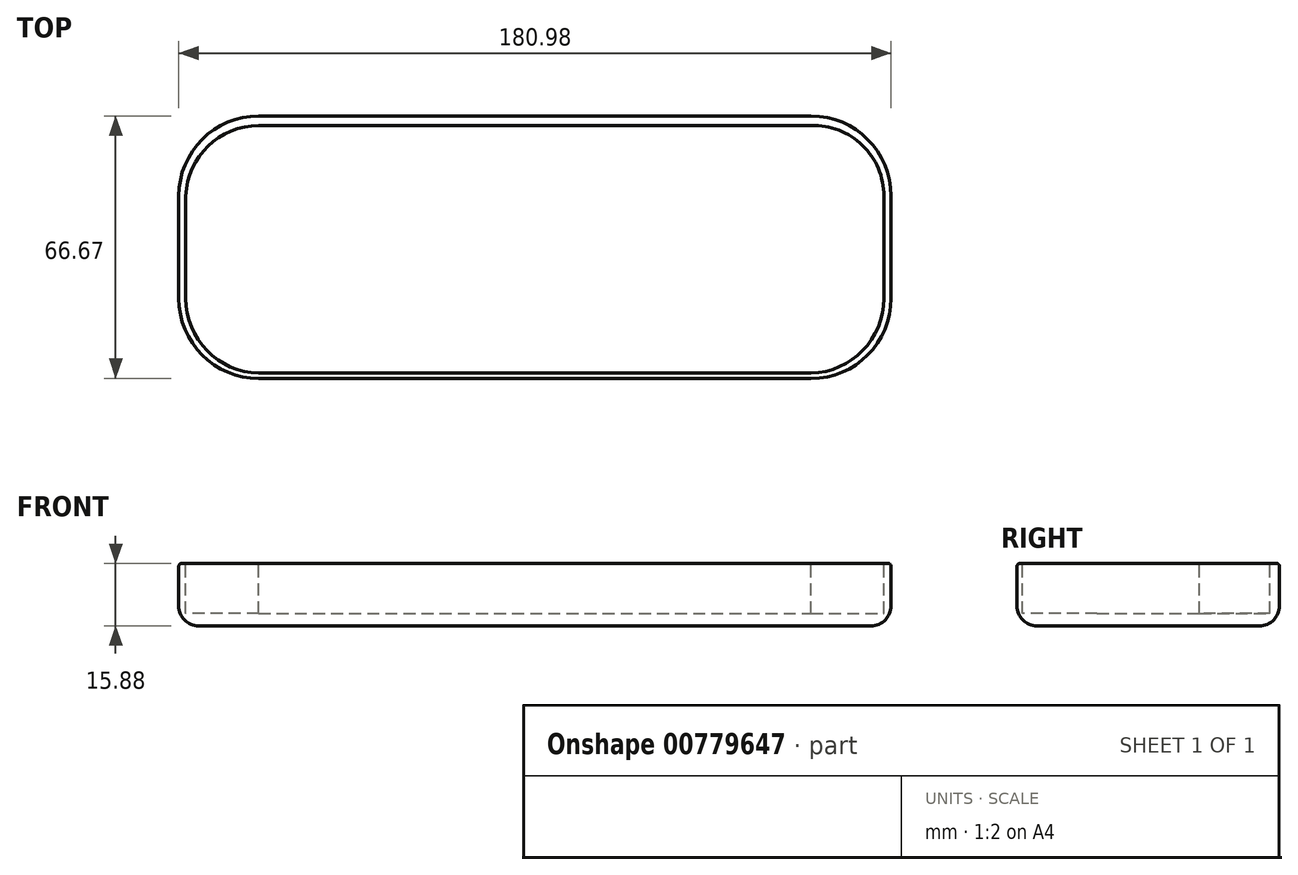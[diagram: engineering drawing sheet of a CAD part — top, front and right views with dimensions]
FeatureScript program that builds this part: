
annotation { "Feature Type Name" : "Feature", "Feature Type Description" : "" }
export const myFeature = defineFeature(function(context is Context, id is Id, definition is map)
    precondition{}
    {
        {
            var Q0;
            Q0=qCreatedBy(makeId("Top.planeOp"),FACE);
            var sketch = newSketch(context, id + "F0", { "sketchPlane" : qUnion([Q0])});
            skLineSegment(sketch, "E0.bottom", {"start": v(-74.66, 3.8) * mm, "end": v(106.32, 3.8) * mm});
            skLineSegment(sketch, "E0.top", {"start": v(-74.66, 70.48) * mm, "end": v(106.32, 70.48) * mm});
            skLineSegment(sketch, "E0.left", {"start": v(-74.66, 3.8) * mm, "end": v(-74.66, 70.48) * mm});
            skLineSegment(sketch, "E0.right", {"start": v(106.32, 3.8) * mm, "end": v(106.32, 70.48) * mm});
            skSolve(sketch);
        }
        {
            var Q0;
            Q0 = qSketchRegion(id + "F0", true);
            extrude(context, id + "F1", {"entities" : qUnion([Q0]), "depth" : 15.88 * mm, "offsetDistance" : 25.4 * mm});
        }
        {
            var Q0;
            Q0=makeQuery(id+"F1.opExtrude","SWEPT_EDGE",EDGE,{"disambiguationData":[OSD([sQuery(id+"F0.wireOp",EDGE,"E0.top"),sQuery(id+"F0.wireOp",EDGE,"E0.right")])]});
            var Q1;
            Q1=makeQuery(id+"F1.opExtrude","SWEPT_EDGE",EDGE,{"disambiguationData":[OSD([sQuery(id+"F0.wireOp",EDGE,"E0.bottom"),sQuery(id+"F0.wireOp",EDGE,"E0.right")])]});
            var Q2;
            Q2=makeQuery(id+"F1.opExtrude","SWEPT_EDGE",EDGE,{"disambiguationData":[OSD([sQuery(id+"F0.wireOp",EDGE,"E0.top"),sQuery(id+"F0.wireOp",EDGE,"E0.left")])]});
            var Q3;
            Q3=makeQuery(id+"F1.opExtrude","SWEPT_EDGE",EDGE,{"disambiguationData":[OSD([sQuery(id+"F0.wireOp",EDGE,"E0.bottom"),sQuery(id+"F0.wireOp",EDGE,"E0.left")])]});
            fillet(context, id + "F2", {"entities" : qUnion([Q0, Q1, Q2, Q3]), "radius" : 20.32 * mm, "tangentPropagation" : true, "allowEdgeOverflow" : false});
        }
        {
            var Q0;
            Q0=makeQuery(id+"F1.opExtrude","CAP_EDGE",EDGE,{"disambiguationData":[OSD([sQuery(id+"F0.wireOp",EDGE,"E0.top")])],"isStart":true});
            fillet(context, id + "F3", {"entities" : qUnion([Q0]), "radius" : 5.08 * mm, "tangentPropagation" : true, "allowEdgeOverflow" : false});
        }
        {
            var Q0;
            Q0=makeQuery(id+"F1.opExtrude","CAP_FACE",FACE,{"disambiguationData":[OSD([sQuery(id+"F0.wireOp",EDGE,"E0.bottom"),sQuery(id+"F0.wireOp",EDGE,"E0.top"),sQuery(id+"F0.wireOp",EDGE,"E0.left"),sQuery(id+"F0.wireOp",EDGE,"E0.right")])],"isStart":false});
            var sketch = newSketch(context, id + "F4", { "sketchPlane" : qUnion([Q0])});
            skLineSegment(sketch, "E1", {"start": v(-54.34, 68.03) * mm, "end": v(86, 68.03) * mm});
            skLineSegment(sketch, "E2", {"start": v(86, 68.03) * mm, "end": v(104.5, 50.16) * mm});
            skLineSegment(sketch, "E3", {"start": v(104.5, 50.16) * mm, "end": v(104.5, 24.13) * mm});
            skLineSegment(sketch, "E4", {"start": v(104.5, 24.13) * mm, "end": v(86, 5.14) * mm});
            skLineSegment(sketch, "E5", {"start": v(86, 5.14) * mm, "end": v(-54.34, 5.14) * mm});
            skLineSegment(sketch, "E6", {"start": v(-54.34, 5.14) * mm, "end": v(-72.85, 24.13) * mm});
            skLineSegment(sketch, "E7", {"start": v(-72.85, 24.13) * mm, "end": v(-72.85, 50.16) * mm});
            skLineSegment(sketch, "E8", {"start": v(-72.85, 50.16) * mm, "end": v(-54.34, 68.03) * mm});
            skSolve(sketch);
        }
        {
            var Q0;
            Q0 = qSketchRegion(id + "F4", true);
            extrude(context, id + "F5", {"entities" : qUnion([Q0]), "operationType" : NewBodyOperationType.REMOVE, "oppositeDirection" : true, "depth" : 12.7 * mm, "offsetDistance" : 25.4 * mm});
        }
        {
            var Q0;
            Q0=makeQuery(id+"F1.opExtrude","CAP_FACE",FACE,{"disambiguationData":[OSD([sQuery(id+"F0.wireOp",EDGE,"E0.bottom"),sQuery(id+"F0.wireOp",EDGE,"E0.top"),sQuery(id+"F0.wireOp",EDGE,"E0.left"),sQuery(id+"F0.wireOp",EDGE,"E0.right")])],"isStart":false});
            var sketch = newSketch(context, id + "F6", { "sketchPlane" : qUnion([Q0])});
            skArc(sketch, "E9", {"start": v(86, 5.14) * mm, "mid": v(99.1, 10.88) * mm, "end": v(104.5, 24.13) * mm});
            skSolve(sketch);
        }
        {
            var Q0;
            Q0=makeQuery(id+"F6.imprint","IMPRINT",FACE,{"disambiguationData":[TD([[makeQuery(id+"F6.imprint","IMPRINT",EDGE,{"derivedFrom":sQuery(id+"F6.wireOp",EDGE,"E9")}),1.0]])]});
            extrude(context, id + "F7", {"entities" : qUnion([Q0]), "operationType" : NewBodyOperationType.REMOVE, "oppositeDirection" : true, "depth" : 12.7 * mm, "offsetDistance" : 25.4 * mm});
        }
        {
            var Q0;
            Q0=makeQuery(id+"F1.opExtrude","CAP_FACE",FACE,{"disambiguationData":[OSD([sQuery(id+"F0.wireOp",EDGE,"E0.bottom"),sQuery(id+"F0.wireOp",EDGE,"E0.top"),sQuery(id+"F0.wireOp",EDGE,"E0.left"),sQuery(id+"F0.wireOp",EDGE,"E0.right")])],"isStart":false});
            var sketch = newSketch(context, id + "F8", { "sketchPlane" : qUnion([Q0])});
            skArc(sketch, "E10", {"start": v(-72.85, 24.13) * mm, "mid": v(-67.46, 10.87) * mm, "end": v(-54.34, 5.14) * mm});
            skSolve(sketch);
        }
        {
            var Q0;
            Q0=makeQuery(id+"F8.imprint","IMPRINT",FACE,{"disambiguationData":[TD([[makeQuery(id+"F8.imprint","IMPRINT",EDGE,{"derivedFrom":sQuery(id+"F8.wireOp",EDGE,"E10")}),1.0]])]});
            extrude(context, id + "F9", {"entities" : qUnion([Q0]), "operationType" : NewBodyOperationType.REMOVE, "oppositeDirection" : true, "depth" : 12.7 * mm, "offsetDistance" : 25.4 * mm});
        }
        {
            var Q0;
            Q0=makeQuery(id+"F1.opExtrude","CAP_FACE",FACE,{"disambiguationData":[OSD([sQuery(id+"F0.wireOp",EDGE,"E0.bottom"),sQuery(id+"F0.wireOp",EDGE,"E0.top"),sQuery(id+"F0.wireOp",EDGE,"E0.left"),sQuery(id+"F0.wireOp",EDGE,"E0.right")])],"isStart":false});
            var sketch = newSketch(context, id + "F10", { "sketchPlane" : qUnion([Q0])});
            skArc(sketch, "E11", {"start": v(-54.34, 68.03) * mm, "mid": v(-67.2, 62.84) * mm, "end": v(-72.85, 50.16) * mm});
            skSolve(sketch);
        }
        {
            var Q0;
            Q0=makeQuery(id+"F10.imprint","IMPRINT",FACE,{"disambiguationData":[TD([[makeQuery(id+"F10.imprint","IMPRINT",EDGE,{"derivedFrom":sQuery(id+"F10.wireOp",EDGE,"E11")}),1.0]])]});
            extrude(context, id + "F11", {"entities" : qUnion([Q0]), "operationType" : NewBodyOperationType.REMOVE, "oppositeDirection" : true, "depth" : 12.7 * mm, "offsetDistance" : 25.4 * mm});
        }
        {
            var Q0;
            Q0=makeQuery(id+"F1.opExtrude","CAP_FACE",FACE,{"disambiguationData":[OSD([sQuery(id+"F0.wireOp",EDGE,"E0.bottom"),sQuery(id+"F0.wireOp",EDGE,"E0.top"),sQuery(id+"F0.wireOp",EDGE,"E0.left"),sQuery(id+"F0.wireOp",EDGE,"E0.right")])],"isStart":false});
            var sketch = newSketch(context, id + "F12", { "sketchPlane" : qUnion([Q0])});
            skArc(sketch, "E12", {"start": v(104.5, 50.16) * mm, "mid": v(99.04, 63.02) * mm, "end": v(86, 68.03) * mm});
            skSolve(sketch);
        }
        {
            var Q0;
            Q0=makeQuery(id+"F12.imprint","IMPRINT",FACE,{"disambiguationData":[TD([[makeQuery(id+"F12.imprint","IMPRINT",EDGE,{"derivedFrom":sQuery(id+"F12.wireOp",EDGE,"E12")}),1.0]])]});
            extrude(context, id + "F13", {"entities" : qUnion([Q0]), "operationType" : NewBodyOperationType.REMOVE, "oppositeDirection" : true, "depth" : 12.7 * mm, "offsetDistance" : 25.4 * mm});
        }
        {
            var Q0;
            Q0=makeQuery(id+"F5.boolean.opBoolean","COPY",EDGE,{"derivedFrom":makeQuery(id+"F5.opExtrude","CAP_EDGE",EDGE,{"disambiguationData":[OSD([sQuery(id+"F4.wireOp",EDGE,"E5")])],"isStart":true})});
            var Q1;
            Q1=makeQuery(id+"F1.opExtrude","CAP_EDGE",EDGE,{"disambiguationData":[OSD([sQuery(id+"F0.wireOp",EDGE,"E0.bottom")])],"isStart":false});
            var Q2;
            Q2=makeQuery(id+"F9.boolean.opBoolean","COPY",EDGE,{"derivedFrom":makeQuery(id+"F9.opExtrude","CAP_EDGE",EDGE,{"disambiguationData":[OSD([sQuery(id+"F8.wireOp",EDGE,"E10")])],"isStart":true})});
            var Q3;
            {var subQ0=sQuery(id+"F0.wireOp",EDGE,"E0.left");var subQ1=sQuery(id+"F0.wireOp",EDGE,"E0.bottom");Q3=makeQuery(id+"F2.opFillet","BLEND_EDGE",EDGE,{"blendedFrom":[makeQuery(id+"F1.opExtrude","SWEPT_EDGE",EDGE,{"disambiguationData":[OSD([subQ1,subQ0])]}),makeQuery(id+"F1.opExtrude","CAP_FACE",FACE,{"disambiguationData":[OSD([subQ1,sQuery(id+"F0.wireOp",EDGE,"E0.top"),subQ0,sQuery(id+"F0.wireOp",EDGE,"E0.right")])],"isStart":false})],"blendedInto":[makeQuery(id+"F1.opExtrude","CAP_FACE",FACE,{"disambiguationData":[OSD([subQ1,sQuery(id+"F0.wireOp",EDGE,"E0.top"),subQ0,sQuery(id+"F0.wireOp",EDGE,"E0.right")])],"isStart":false})]});}
            var Q4;
            Q4=makeQuery(id+"F5.boolean.opBoolean","COPY",EDGE,{"derivedFrom":makeQuery(id+"F5.opExtrude","CAP_EDGE",EDGE,{"disambiguationData":[OSD([sQuery(id+"F4.wireOp",EDGE,"E7")])],"isStart":true})});
            var Q5;
            Q5=makeQuery(id+"F1.opExtrude","CAP_EDGE",EDGE,{"disambiguationData":[OSD([sQuery(id+"F0.wireOp",EDGE,"E0.left")])],"isStart":false});
            var Q6;
            {var subQ0=sQuery(id+"F0.wireOp",EDGE,"E0.left");var subQ1=sQuery(id+"F0.wireOp",EDGE,"E0.top");Q6=makeQuery(id+"F2.opFillet","BLEND_EDGE",EDGE,{"blendedFrom":[makeQuery(id+"F1.opExtrude","SWEPT_EDGE",EDGE,{"disambiguationData":[OSD([subQ1,subQ0])]}),makeQuery(id+"F1.opExtrude","CAP_FACE",FACE,{"disambiguationData":[OSD([sQuery(id+"F0.wireOp",EDGE,"E0.bottom"),subQ1,subQ0,sQuery(id+"F0.wireOp",EDGE,"E0.right")])],"isStart":false})],"blendedInto":[makeQuery(id+"F1.opExtrude","CAP_FACE",FACE,{"disambiguationData":[OSD([sQuery(id+"F0.wireOp",EDGE,"E0.bottom"),subQ1,subQ0,sQuery(id+"F0.wireOp",EDGE,"E0.right")])],"isStart":false})]});}
            var Q7;
            Q7=makeQuery(id+"F11.boolean.opBoolean","COPY",EDGE,{"derivedFrom":makeQuery(id+"F11.opExtrude","CAP_EDGE",EDGE,{"disambiguationData":[OSD([sQuery(id+"F10.wireOp",EDGE,"E11")])],"isStart":true})});
            var Q8;
            Q8=makeQuery(id+"F1.opExtrude","CAP_EDGE",EDGE,{"disambiguationData":[OSD([sQuery(id+"F0.wireOp",EDGE,"E0.top")])],"isStart":false});
            var Q9;
            Q9=makeQuery(id+"F5.boolean.opBoolean","COPY",EDGE,{"derivedFrom":makeQuery(id+"F5.opExtrude","CAP_EDGE",EDGE,{"disambiguationData":[OSD([sQuery(id+"F4.wireOp",EDGE,"E1")])],"isStart":true})});
            var Q10;
            Q10=makeQuery(id+"F13.boolean.opBoolean","COPY",EDGE,{"derivedFrom":makeQuery(id+"F13.opExtrude","CAP_EDGE",EDGE,{"disambiguationData":[OSD([sQuery(id+"F12.wireOp",EDGE,"E12")])],"isStart":true})});
            var Q11;
            {var subQ0=sQuery(id+"F0.wireOp",EDGE,"E0.right");var subQ1=sQuery(id+"F0.wireOp",EDGE,"E0.top");Q11=makeQuery(id+"F2.opFillet","BLEND_EDGE",EDGE,{"blendedFrom":[makeQuery(id+"F1.opExtrude","SWEPT_EDGE",EDGE,{"disambiguationData":[OSD([subQ1,subQ0])]}),makeQuery(id+"F1.opExtrude","CAP_FACE",FACE,{"disambiguationData":[OSD([sQuery(id+"F0.wireOp",EDGE,"E0.bottom"),subQ1,sQuery(id+"F0.wireOp",EDGE,"E0.left"),subQ0])],"isStart":false})],"blendedInto":[makeQuery(id+"F1.opExtrude","CAP_FACE",FACE,{"disambiguationData":[OSD([sQuery(id+"F0.wireOp",EDGE,"E0.bottom"),subQ1,sQuery(id+"F0.wireOp",EDGE,"E0.left"),subQ0])],"isStart":false})]});}
            var Q12;
            Q12=makeQuery(id+"F5.boolean.opBoolean","COPY",EDGE,{"derivedFrom":makeQuery(id+"F5.opExtrude","CAP_EDGE",EDGE,{"disambiguationData":[OSD([sQuery(id+"F4.wireOp",EDGE,"E3")])],"isStart":true})});
            var Q13;
            Q13=makeQuery(id+"F1.opExtrude","CAP_EDGE",EDGE,{"disambiguationData":[OSD([sQuery(id+"F0.wireOp",EDGE,"E0.right")])],"isStart":false});
            var Q14;
            Q14=makeQuery(id+"F7.boolean.opBoolean","COPY",EDGE,{"derivedFrom":makeQuery(id+"F7.opExtrude","CAP_EDGE",EDGE,{"disambiguationData":[OSD([sQuery(id+"F6.wireOp",EDGE,"E9")])],"isStart":true})});
            var Q15;
            {var subQ0=sQuery(id+"F0.wireOp",EDGE,"E0.right");var subQ1=sQuery(id+"F0.wireOp",EDGE,"E0.bottom");Q15=makeQuery(id+"F2.opFillet","BLEND_EDGE",EDGE,{"blendedFrom":[makeQuery(id+"F1.opExtrude","SWEPT_EDGE",EDGE,{"disambiguationData":[OSD([subQ1,subQ0])]}),makeQuery(id+"F1.opExtrude","CAP_FACE",FACE,{"disambiguationData":[OSD([subQ1,sQuery(id+"F0.wireOp",EDGE,"E0.top"),sQuery(id+"F0.wireOp",EDGE,"E0.left"),subQ0])],"isStart":false})],"blendedInto":[makeQuery(id+"F1.opExtrude","CAP_FACE",FACE,{"disambiguationData":[OSD([subQ1,sQuery(id+"F0.wireOp",EDGE,"E0.top"),sQuery(id+"F0.wireOp",EDGE,"E0.left"),subQ0])],"isStart":false})]});}
            fillet(context, id + "F14", {"entities" : qUnion([Q0, Q1, Q2, Q3, Q4, Q5, Q6, Q7, Q8, Q9, Q10, Q11, Q12, Q13, Q14, Q15]), "radius" : 0.76 * mm, "tangentPropagation" : true, "allowEdgeOverflow" : false});
        }
    });
